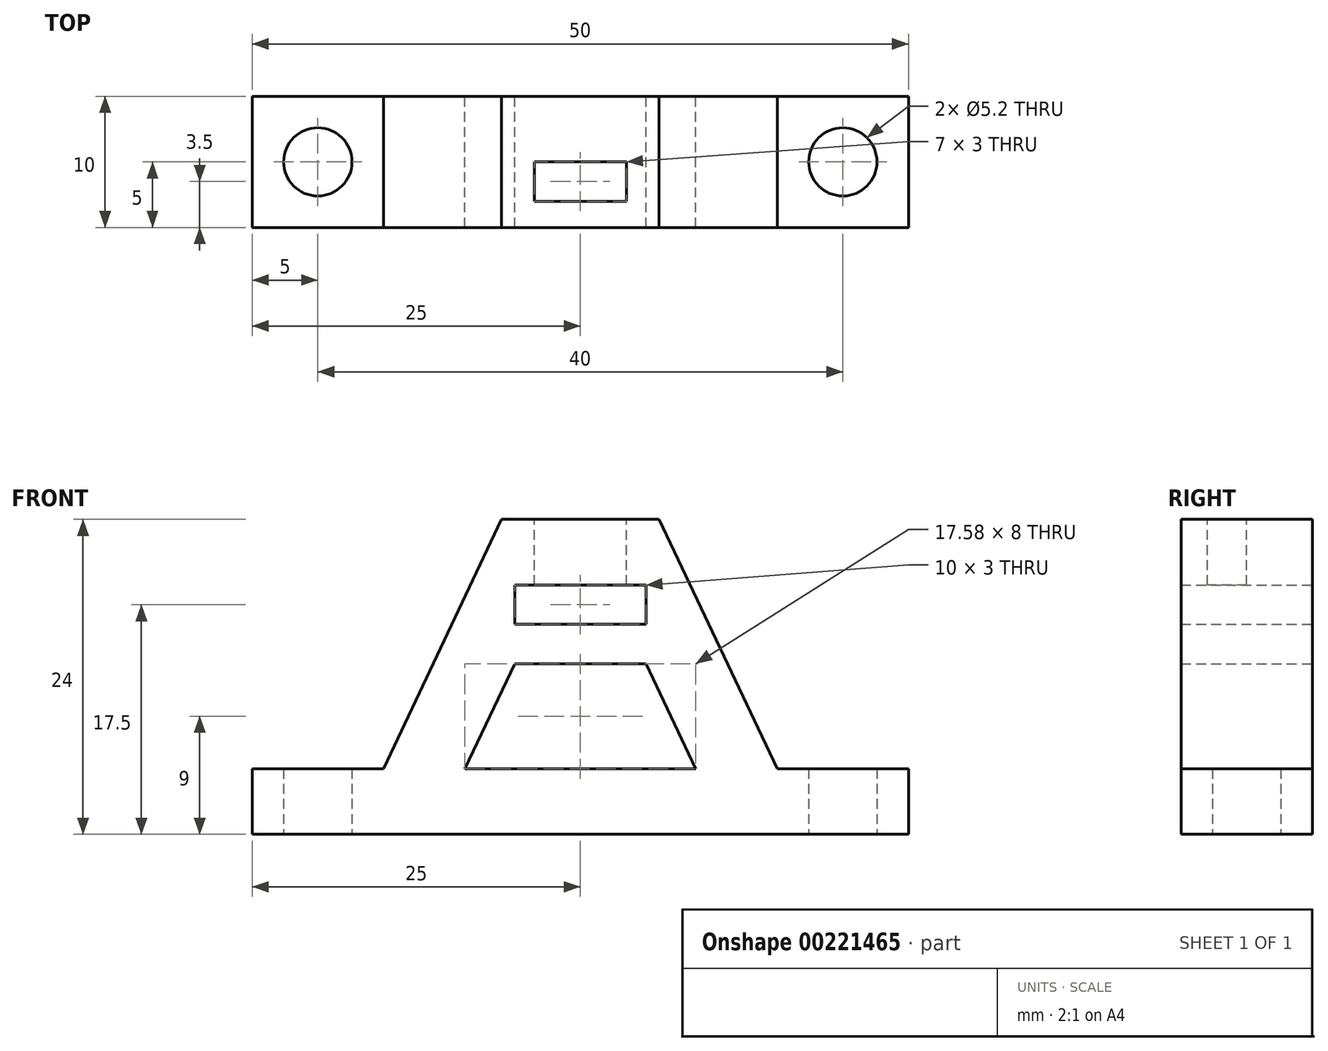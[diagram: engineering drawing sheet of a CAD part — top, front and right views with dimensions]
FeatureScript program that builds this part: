
annotation { "Feature Type Name" : "Feature", "Feature Type Description" : "" }
export const myFeature = defineFeature(function(context is Context, id is Id, definition is map)
    precondition{}
    {
        {
            var Q0;
            Q0=qCreatedBy(makeId("Top.planeOp"),FACE);
            var sketch = newSketch(context, id + "F0", { "sketchPlane" : qUnion([Q0])});
            skCircle(sketch, "E0", {"center": v(0, 0) * mm, "radius": 2.6 * mm});
            skCircle(sketch, "E1", {"center": v(40, 0) * mm, "radius": 2.6 * mm});
            skLineSegment(sketch, "E2.bottom", {"start": v(-5, 5) * mm, "end": v(45, 5) * mm});
            skLineSegment(sketch, "E2.top", {"start": v(-5, -5) * mm, "end": v(45, -5) * mm});
            skLineSegment(sketch, "E2.left", {"start": v(-5, 5) * mm, "end": v(-5, -5) * mm});
            skLineSegment(sketch, "E2.right", {"start": v(45, 5) * mm, "end": v(45, -5) * mm});
            skPoint(sketch, "E3", {"position": v(-5, 0) * mm});
            skSolve(sketch);
        }
        {
            var Q0;
            Q0=makeQuery(id+"F0.imprint","IMPRINT",FACE,{"disambiguationData":[TD([[makeQuery(id+"F0.imprint","IMPRINT",EDGE,{"derivedFrom":sQuery(id+"F0.wireOp",EDGE,"E0")}),-1.0]])]});
            extrude(context, id + "F1", {"entities" : qUnion([Q0]), "depth" : 5 * mm});
        }
        {
            var Q0;
            Q0=makeQuery(id+"F1.opExtrude","SWEPT_FACE",FACE,{"disambiguationData":[OSD([sQuery(id+"F0.wireOp",EDGE,"E2.bottom")])]});
            var sketch = newSketch(context, id + "F2", { "sketchPlane" : qUnion([Q0])});
            skLineSegment(sketch, "E4", {"start": v(-20, 0) * mm, "end": v(-20, 24) * mm, "construction": true});
            skPoint(sketch, "E4.endSnap0", {"position": v(-20, 0) * mm});
            skLineSegment(sketch, "E5", {"start": v(-5, 5) * mm, "end": v(-14, 24) * mm});
            skLineSegment(sketch, "E6", {"start": v(-14, 24) * mm, "end": v(-20, 24) * mm});
            skLineSegment(sketch, "E7.MirrorCS", {"start": v(-26, 24) * mm, "end": v(-20, 24) * mm});
            skLineSegment(sketch, "E8.MirrorCS", {"start": v(-35, 5) * mm, "end": v(-26, 24) * mm});
            skLineSegment(sketch, "E9", {"start": v(-5, 5) * mm, "end": v(-35, 5) * mm});
            skLineSegment(sketch, "E10.bottom", {"start": v(-15, 16) * mm, "end": v(-25, 16) * mm});
            skLineSegment(sketch, "E10.top", {"start": v(-15, 19) * mm, "end": v(-25, 19) * mm});
            skLineSegment(sketch, "E10.left", {"start": v(-15, 16) * mm, "end": v(-15, 19) * mm});
            skLineSegment(sketch, "E10.right", {"start": v(-25, 16) * mm, "end": v(-25, 19) * mm});
            skPoint(sketch, "E11", {"position": v(-20, 16) * mm});
            skSolve(sketch);
        }
        {
            var Q0;
            Q0=makeQuery(id+"F2.imprint","IMPRINT",FACE,{"disambiguationData":[TD([[makeQuery(id+"F2.imprint","IMPRINT",EDGE,{"derivedFrom":sQuery(id+"F2.wireOp",EDGE,"E5")}),1.0]])]});
            extrude(context, id + "F3", {"entities" : qUnion([Q0]), "operationType" : NewBodyOperationType.ADD, "oppositeDirection" : true, "depth" : 10 * mm});
        }
        {
            var Q0;
            Q0=makeQuery(id+"F3.opExtrude","SWEPT_FACE",FACE,{"disambiguationData":[OSD([sQuery(id+"F2.wireOp",EDGE,"E6"),sQuery(id+"F2.wireOp",EDGE,"E7.MirrorCS")])]});
            var sketch = newSketch(context, id + "F4", { "sketchPlane" : qUnion([Q0])});
            skLineSegment(sketch, "E12.bottom", {"start": v(16.5, 0) * mm, "end": v(23.5, 0) * mm});
            skLineSegment(sketch, "E12.top", {"start": v(16.5, -3) * mm, "end": v(23.5, -3) * mm});
            skLineSegment(sketch, "E12.left", {"start": v(16.5, 0) * mm, "end": v(16.5, -3) * mm});
            skLineSegment(sketch, "E12.right", {"start": v(23.5, 0) * mm, "end": v(23.5, -3) * mm});
            skPoint(sketch, "E13", {"position": v(20, 0) * mm});
            skPoint(sketch, "E14", {"position": v(20, 5) * mm});
            skPoint(sketch, "E15", {"position": v(14, 0) * mm});
            skSolve(sketch);
        }
        {
            var Q0;
            Q0=makeQuery(id+"F4.imprint","IMPRINT",FACE,{"disambiguationData":[TD([[makeQuery(id+"F4.imprint","IMPRINT",EDGE,{"derivedFrom":sQuery(id+"F4.wireOp",EDGE,"E12.bottom")}),-1.0]])]});
            extrude(context, id + "F5", {"entities" : qUnion([Q0]), "operationType" : NewBodyOperationType.REMOVE, "oppositeDirection" : true, "depth" : 8 * mm});
        }
        {
            var Q0;
            Q0=makeQuery(id+"F3.boolean.opBoolean","MERGE",FACE,{"derivedFrom":[makeQuery(id+"F1.opExtrude","SWEPT_FACE",FACE,{"disambiguationData":[OSD([sQuery(id+"F0.wireOp",EDGE,"E2.bottom")])]}),makeQuery(id+"F3.opExtrude","CAP_FACE",FACE,{"disambiguationData":[OSD([sQuery(id+"F2.wireOp",EDGE,"E5"),sQuery(id+"F2.wireOp",EDGE,"E6"),sQuery(id+"F2.wireOp",EDGE,"E7.MirrorCS"),sQuery(id+"F2.wireOp",EDGE,"E8.MirrorCS"),sQuery(id+"F2.wireOp",EDGE,"E9"),sQuery(id+"F2.wireOp",EDGE,"E10.bottom"),sQuery(id+"F2.wireOp",EDGE,"E10.top"),sQuery(id+"F2.wireOp",EDGE,"E10.left"),sQuery(id+"F2.wireOp",EDGE,"E10.right")])],"isStart":true})]});
            var sketch = newSketch(context, id + "F6", { "sketchPlane" : qUnion([Q0])});
            skLineSegment(sketch, "E16", {"start": v(-25, 13) * mm, "end": v(-28.79, 5) * mm});
            skLineSegment(sketch, "E17", {"start": v(-28.79, 5) * mm, "end": v(-11.21, 5) * mm});
            skLineSegment(sketch, "E18", {"start": v(-11.21, 5) * mm, "end": v(-15, 13) * mm});
            skLineSegment(sketch, "E19", {"start": v(-15, 13) * mm, "end": v(-25, 13) * mm});
            skPoint(sketch, "E20", {"position": v(-20, 16) * mm});
            skPoint(sketch, "E21", {"position": v(-20, 13) * mm});
            skSolve(sketch);
        }
        {
            var Q0;
            Q0=makeQuery(id+"F6.imprint","IMPRINT",FACE,{"disambiguationData":[TD([[makeQuery(id+"F6.imprint","IMPRINT",EDGE,{"derivedFrom":sQuery(id+"F6.wireOp",EDGE,"E16")}),1.0]])]});
            var Q1;
            Q1=makeQuery(id+"F3.boolean.opBoolean","MERGE",FACE,{"derivedFrom":[makeQuery(id+"F1.opExtrude","SWEPT_FACE",FACE,{"disambiguationData":[OSD([sQuery(id+"F0.wireOp",EDGE,"E2.top")])]}),makeQuery(id+"F3.opExtrude","CAP_FACE",FACE,{"disambiguationData":[OSD([sQuery(id+"F2.wireOp",EDGE,"E5"),sQuery(id+"F2.wireOp",EDGE,"E6"),sQuery(id+"F2.wireOp",EDGE,"E7.MirrorCS"),sQuery(id+"F2.wireOp",EDGE,"E8.MirrorCS"),sQuery(id+"F2.wireOp",EDGE,"E9"),sQuery(id+"F2.wireOp",EDGE,"E10.bottom"),sQuery(id+"F2.wireOp",EDGE,"E10.top"),sQuery(id+"F2.wireOp",EDGE,"E10.left"),sQuery(id+"F2.wireOp",EDGE,"E10.right")])],"isStart":false})]});
            extrude(context, id + "F7", {"entities" : qUnion([Q0]), "operationType" : NewBodyOperationType.REMOVE, "endBound" : BoundingType.UP_TO_SURFACE, "oppositeDirection" : true, "endBoundEntityFace" : qUnion([Q1]), "depth" : 25 * mm});
        }
    });
